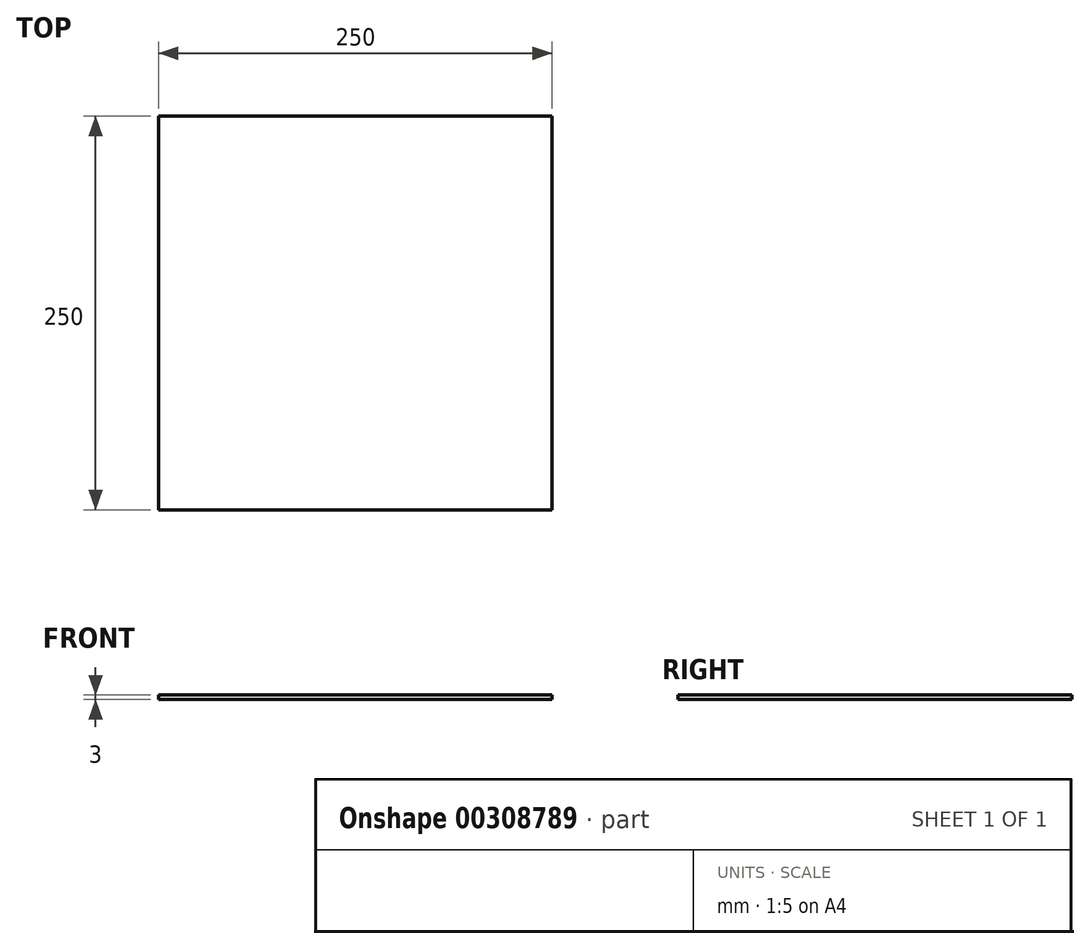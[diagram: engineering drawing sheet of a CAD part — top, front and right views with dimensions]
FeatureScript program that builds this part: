
annotation { "Feature Type Name" : "Feature", "Feature Type Description" : "" }
export const myFeature = defineFeature(function(context is Context, id is Id, definition is map)
    precondition{}
    {
        {
            var Q0;
            Q0=qCreatedBy(makeId("Top.planeOp"),FACE);
            var sketch = newSketch(context, id + "F0", { "sketchPlane" : qUnion([Q0])});
            skLineSegment(sketch, "E0.bottom", {"start": v(125, -125) * mm, "end": v(-125, -125) * mm});
            skLineSegment(sketch, "E0.top", {"start": v(125, 125) * mm, "end": v(-125, 125) * mm});
            skLineSegment(sketch, "E0.left", {"start": v(125, -125) * mm, "end": v(125, 125) * mm});
            skLineSegment(sketch, "E0.right", {"start": v(-125, -125) * mm, "end": v(-125, 125) * mm});
            skPoint(sketch, "E0.middle", {"position": v(0, 0) * mm});
            skSolve(sketch);
        }
        {
            var Q0;
            Q0 = qSketchRegion(id + "F0", true);
            extrude(context, id + "F1", {"entities" : qUnion([Q0]), "depth" : 3 * mm});
        }
    });
